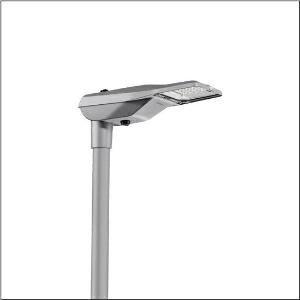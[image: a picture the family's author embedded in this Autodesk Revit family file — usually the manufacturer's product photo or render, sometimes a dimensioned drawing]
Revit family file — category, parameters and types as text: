
# Revit family: streetlight_sl_21_iq_micro___st1_0a_5xe1d41y08db_7ab9
name_source: partatom
category: Lighting Fixtures
units: mm (PartAtom-declared; Revit-internal decimal feet)

## family parameters
Cut with Voids When Loaded = No
Host = Face
Light Source = No
Part Type = Normal
Room Calculation Point = No
Round Connector Dimension = Use Diameter
Shared = No

## types (1)
- --- (1 x LED, 5280 lm, 39.1 W, 4000K)
    Apparent Load = 39 VA
    CIE Flux Codes = 37 72 97 100 100
    Color Rendering = 70
    Color Temperature = 4000K
    Default Elevation = 1800 mm
    Description = Streetlight SL 21 iQ micro, mast luminaire, primary light control with lens, of PMMA, primary optical cover: cover, of toughened safety glass, transparent, light distribution: ST1.0a, light emission: direct distribution, primary light characteristic: asymmetric, installation type: post-top, side-entry, LED, High Power LED, rated luminous flux: 5.280lm, luminous efficacy: 135lm/W, light colour: 740, colour temperature: 4000K, control: presetting dimming logarithmic, Street-Remote, Auto-Match, Temp-Guard, Lumen-Switch, Night-Set, Smart-Wire, Light-Fading, Desk-Remote (wireless, voltage-free reading and setting of iQ features in the workshop via application-optimized NFC function/RFID function), optimised constant luminous flux control (CLO 2.0), mains connection: 220..240V, AC, 50/60Hz, start of lifetime: 39W, end of service life: 41W, reduction: 17W, luminaire housing, of diecast aluminium, powder-coated, Siteco® metallic grey (DB 702S), corrosivity category C5 mid according to DIN EN ISO 12944, please order mast flange separately, inclination adjustable: 0°, 5°, 10°, 15°, sealing non-destructively replaceable, multi-level sealing system, length: 528mm, width: 235mm, height: 110mm, mast flange for spigot size: 42mm (side-entry): 5XC10008XM4, 60/48mm (side-entry/post-top): 5XC10108XM2, 76/60mm (side-entry/post-top): 5XC10108XM1, Smart Interface below and above, protection rating (complete): IP66, insulation class (complete): insulation class II (safety insulation), certification: CE, ENEC, ENEC+, VDE, impact resistance: IK09, permissible operating ambient temperature for outdoor applications: -40..+50°C, standard-compliant lighting for roads and squares, packaging unit: 1 piece

Light Distribution: ST1.0a
    Height = 110 mm
    Lamp = 1 x LED
    Lamp Light Flux = 5280 lm
    Lamp Power = 39.1 W
    Lamp count = 1
    Length = 528 mm
    Luminous efficacy = 135 lm/W
    Manufacturer = Siteco
    ModVariant = No
    Model = 5XE1D41Y08DB
    Number of Poles = 1
    OnlyDefault = Yes
    Power Factor = 1
    Product Name = Streetlight SL 21 iQ micro | ST1.0a
    Product group = mast luminaire | pylon top
    ProductGroupID = 6100
    Protection Class = Protection class II
    Protection Degree = IP 66
    RLX_Detail_Level = 1
    RLX_Emergency_Light_Flux = 0 lm
    RLX_Emergency_Type = 0
    RLX_Emergency_Type_DB = No
    RlxData = <blob elided: 98533 chars, md5=dc800bbf>
    Socket = socket
    Standby Power = 0 W
    System Light Flux = 5280 lm
    System Power = 39 W
    Type Comments = factory setting: luminous flux: 100 % | dim-lin: 254 | 765 mA
    Type Image = l_1007239.jpg
    URL = http://relux.com
    VarID = @adj_045305
    Voltage = 0 V
    Weight = 0.00 kg
    Width = 235 mm

## geometry (parser evidence)
native form markers: Blend x4, Sweep x9
no freeform markers — native parametric forms only
